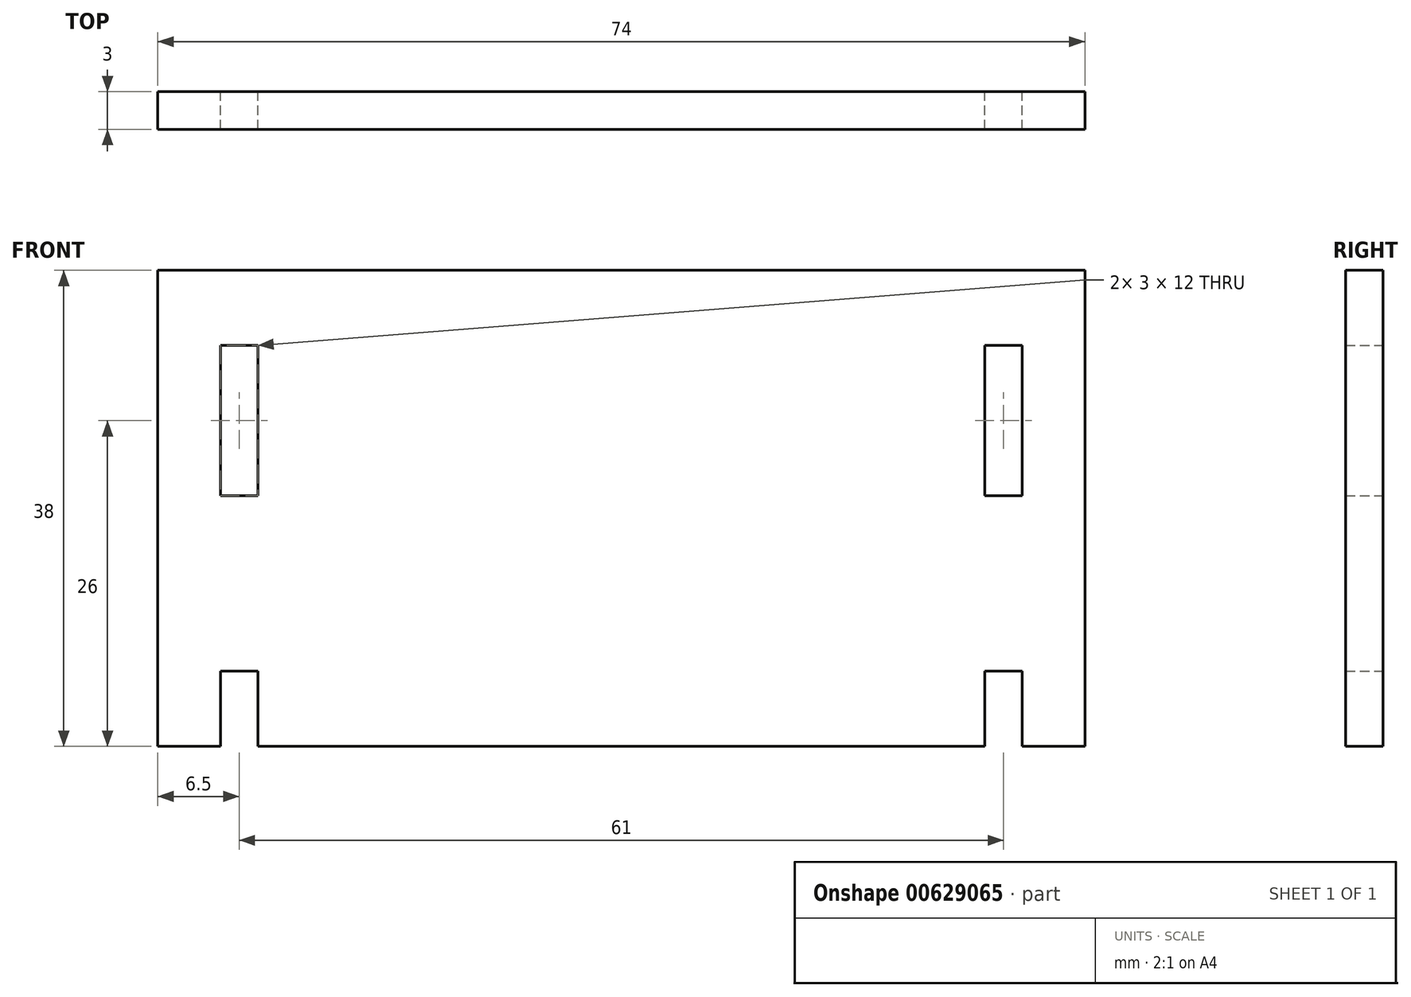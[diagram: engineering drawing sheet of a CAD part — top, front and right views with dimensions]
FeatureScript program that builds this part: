
annotation { "Feature Type Name" : "Feature", "Feature Type Description" : "" }
export const myFeature = defineFeature(function(context is Context, id is Id, definition is map)
    precondition{}
    {
        {
            var Q0;
            Q0=qCreatedBy(makeId("Front.planeOp"),FACE);
            var sketch = newSketch(context, id + "F0", { "sketchPlane" : qUnion([Q0])});
            skLineSegment(sketch, "E0", {"start": v(0, 50.4) * mm, "end": v(0, -34.26) * mm, "construction": true});
            skLineSegment(sketch, "E1", {"start": v(-55.88, 0) * mm, "end": v(55.88, 0) * mm, "construction": true});
            skLineSegment(sketch, "E2.bottom", {"start": v(-37, 28) * mm, "end": v(37, 28) * mm});
            skLineSegment(sketch, "E2.top", {"start": v(-37, -10) * mm, "end": v(-32, -10) * mm});
            skLineSegment(sketch, "E2.left", {"start": v(-37, 28) * mm, "end": v(-37, -10) * mm});
            skLineSegment(sketch, "E2.right", {"start": v(37, 28) * mm, "end": v(37, -10) * mm});
            skLineSegment(sketch, "E3.bottom", {"start": v(-32, 22) * mm, "end": v(-29, 22) * mm});
            skLineSegment(sketch, "E3.top", {"start": v(-32, 10) * mm, "end": v(-29, 10) * mm});
            skLineSegment(sketch, "E3.left", {"start": v(-32, 22) * mm, "end": v(-32, 10) * mm});
            skLineSegment(sketch, "E3.right", {"start": v(-29, 22) * mm, "end": v(-29, 10) * mm});
            skLineSegment(sketch, "E4.bottom", {"start": v(-32, -4) * mm, "end": v(-29, -4) * mm});
            skLineSegment(sketch, "E4.left", {"start": v(-32, -4) * mm, "end": v(-32, -10) * mm});
            skLineSegment(sketch, "E4.right", {"start": v(-29, -4) * mm, "end": v(-29, -10) * mm});
            skLineSegment(sketch, "E5.trimOffspring", {"start": v(-29, -10) * mm, "end": v(29, -10) * mm});
            skLineSegment(sketch, "E6.MirrorCS", {"start": v(29, -10) * mm, "end": v(-29, -10) * mm});
            skLineSegment(sketch, "E7.MirrorCS", {"start": v(29, -4) * mm, "end": v(29, -10) * mm});
            skLineSegment(sketch, "E8.MirrorCS", {"start": v(32, -4) * mm, "end": v(32, -10) * mm});
            skLineSegment(sketch, "E9.MirrorCS", {"start": v(37, -10) * mm, "end": v(32, -10) * mm});
            skLineSegment(sketch, "E10.MirrorCS", {"start": v(32, -4) * mm, "end": v(29, -4) * mm});
            skLineSegment(sketch, "E11.MirrorCS", {"start": v(29, 22) * mm, "end": v(29, 10) * mm});
            skLineSegment(sketch, "E12.MirrorCS", {"start": v(32, 22) * mm, "end": v(32, 10) * mm});
            skLineSegment(sketch, "E13.MirrorCS", {"start": v(32, 10) * mm, "end": v(29, 10) * mm});
            skLineSegment(sketch, "E14.MirrorCS", {"start": v(32, 22) * mm, "end": v(29, 22) * mm});
            skLineSegment(sketch, "E15.MirrorCS", {"start": v(55.88, 0) * mm, "end": v(-55.88, 0) * mm, "construction": true});
            skLineSegment(sketch, "E16.trimOffspring", {"start": v(32, -10) * mm, "end": v(37, -10) * mm});
            skLineSegment(sketch, "E17.trimOffspring", {"start": v(-32, -10) * mm, "end": v(-37, -10) * mm});
            skSolve(sketch);
        }
        {
            var Q0;
            Q0=qSketchRegion(id+"F0",true);
            extrude(context, id + "F1", {"entities" : qUnion([Q0]), "endBound" : BoundingType.SYMMETRIC, "depth" : 3 * mm, "offsetDistance" : 25 * mm});
        }
    });
